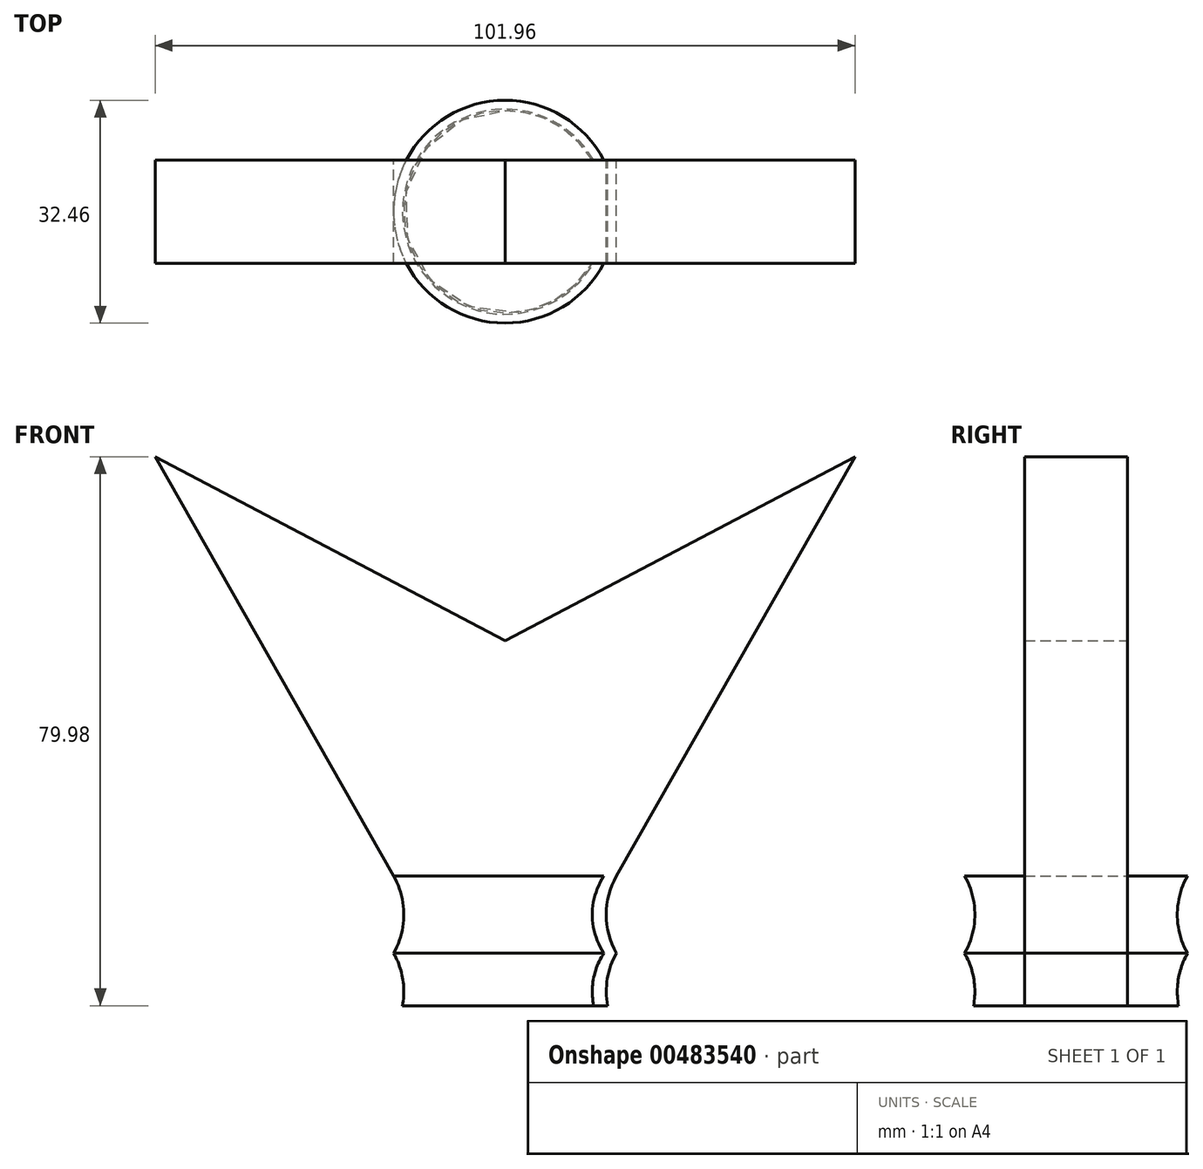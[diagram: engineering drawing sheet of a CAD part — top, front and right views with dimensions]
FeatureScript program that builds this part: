
annotation { "Feature Type Name" : "Feature", "Feature Type Description" : "" }
export const myFeature = defineFeature(function(context is Context, id is Id, definition is map)
    precondition{}
    {
        {
            var Q0;
            Q0=qCreatedBy(makeId("Front.planeOp"),FACE);
            var sketch = newSketch(context, id + "F0", { "sketchPlane" : qUnion([Q0])});
            skLineSegment(sketch, "E0", {"start": v(0, 0) * mm, "end": v(16.23, 0) * mm});
            skLineSegment(sketch, "E1", {"start": v(16.23, 0) * mm, "end": v(50.98, 61.1) * mm});
            skLineSegment(sketch, "E2", {"start": v(50.98, 61.1) * mm, "end": v(0, 34.32) * mm});
            skLineSegment(sketch, "E3.MirrorCS", {"start": v(-50.98, 61.1) * mm, "end": v(0, 34.32) * mm});
            skLineSegment(sketch, "E4.MirrorCS", {"start": v(-16.23, 0) * mm, "end": v(-50.98, 61.1) * mm});
            skLineSegment(sketch, "E5.MirrorCS", {"start": v(0, 0) * mm, "end": v(-16.23, 0) * mm});
            skArc(sketch, "E6", {"start": v(16.23, 0) * mm, "mid": v(14.75, -5.62) * mm, "end": v(16.23, -11.23) * mm});
            skLineSegment(sketch, "E7", {"start": v(31.9, -11.23) * mm, "end": v(-21.36, -11.23) * mm, "construction": true});
            skArc(sketch, "E8", {"start": v(16.23, -11.23) * mm, "mid": v(14.9, -14.95) * mm, "end": v(14.93, -18.9) * mm});
            skLineSegment(sketch, "E9", {"start": v(14.93, -18.9) * mm, "end": v(0, -18.9) * mm});
            skLineSegment(sketch, "E10", {"start": v(0, -18.9) * mm, "end": v(0, 0) * mm});
            skSolve(sketch);
        }
        {
            var Q0;
            Q0=makeQuery(id+"F0.imprint","IMPRINT",FACE,{"disambiguationData":[TD([[makeQuery(id+"F0.imprint","IMPRINT",EDGE,{"derivedFrom":sQuery(id+"F0.wireOp",EDGE,"E0")}),-1.0]])]});
            var Q1;
            Q1=sQuery(id+"F0.wireOp",EDGE,"E10");
            revolve(context, id + "F1", {"entities" : qUnion([Q0]), "axis" : qUnion([Q1]), "revolveType" : RevolveType.FULL});
        }
        {
            var Q0;
            Q0 = qSketchRegion(id + "F0", true);
            extrude(context, id + "F2", {"entities" : qUnion([Q0]), "operationType" : NewBodyOperationType.ADD, "endBound" : BoundingType.SYMMETRIC, "depth" : 15 * mm});
        }
    });
